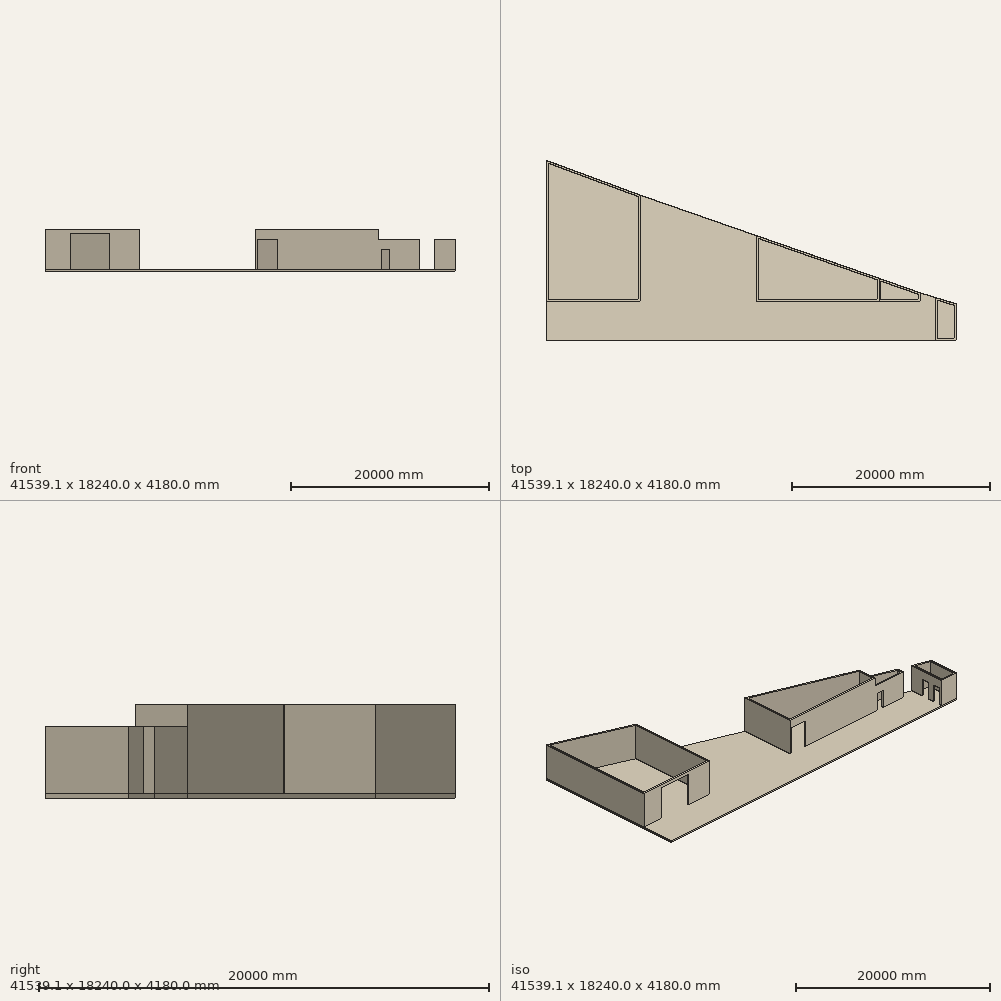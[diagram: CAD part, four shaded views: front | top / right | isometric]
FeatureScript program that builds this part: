
annotation { "Feature Type Name" : "Feature", "Feature Type Description" : "" }
export const myFeature = defineFeature(function(context is Context, id is Id, definition is map)
    precondition{}
    {
        {
            var Q0;
            Q0=qCreatedBy(makeId("Top.planeOp"),FACE);
            var sketch = newSketch(context, id + "F0", { "sketchPlane" : qUnion([Q0])});
            skLineSegment(sketch, "E0", {"start": v(-6364.4, -7586.4) * mm, "end": v(3195.6, -7586.4) * mm});
            skLineSegment(sketch, "E1", {"start": v(3195.6, -7586.4) * mm, "end": v(3195.6, 3113.6) * mm});
            skLineSegment(sketch, "E2", {"start": v(3195.6, 3113.6) * mm, "end": v(-6364.4, 6653.6) * mm});
            skLineSegment(sketch, "E3", {"start": v(-6364.4, 6653.6) * mm, "end": v(-6364.4, -7586.4) * mm});
            skLineSegment(sketch, "E4", {"start": v(14943.68, -976.4) * mm, "end": v(27323.68, -5286.4) * mm});
            skLineSegment(sketch, "E5", {"start": v(27323.68, -5286.4) * mm, "end": v(27323.68, -7586.4) * mm});
            skLineSegment(sketch, "E6", {"start": v(27323.68, -7586.4) * mm, "end": v(14943.68, -7586.4) * mm});
            skLineSegment(sketch, "E7", {"start": v(14943.68, -7586.4) * mm, "end": v(14943.68, -976.4) * mm});
            skLineSegment(sketch, "E8", {"start": v(3195.6, 3113.6) * mm, "end": v(14943.68, -976.4) * mm});
            skLineSegment(sketch, "E9", {"start": v(3195.6, -7586.4) * mm, "end": v(14943.68, -7586.4) * mm});
            skLineSegment(sketch, "E10", {"start": v(27323.68, -5286.4) * mm, "end": v(31493.68, -6756.4) * mm});
            skLineSegment(sketch, "E11", {"start": v(31493.68, -6756.4) * mm, "end": v(31493.68, -7586.4) * mm});
            skLineSegment(sketch, "E12", {"start": v(31493.68, -7586.4) * mm, "end": v(27323.68, -7586.4) * mm});
            skLineSegment(sketch, "E13", {"start": v(33024.74, -7226.4) * mm, "end": v(35174.74, -7886.4) * mm});
            skLineSegment(sketch, "E14", {"start": v(35174.74, -7886.4) * mm, "end": v(35174.74, -11586.4) * mm});
            skLineSegment(sketch, "E15", {"start": v(35174.74, -11586.4) * mm, "end": v(33024.74, -11586.4) * mm});
            skLineSegment(sketch, "E16", {"start": v(33024.74, -11586.4) * mm, "end": v(33024.74, -7226.4) * mm});
            skLineSegment(sketch, "E17", {"start": v(33024.74, -7226.4) * mm, "end": v(31493.68, -6756.4) * mm});
            skLineSegment(sketch, "E18", {"start": v(33024.74, -11586.4) * mm, "end": v(-6364.4, -11586.4) * mm});
            skLineSegment(sketch, "E19", {"start": v(-6364.4, -11586.4) * mm, "end": v(-6364.4, -7586.4) * mm});
            skSolve(sketch);
        }
        {
            var Q0;
            Q0=makeQuery(id+"F0.imprint","IMPRINT",FACE,{"disambiguationData":[TD([[makeQuery(id+"F0.imprint","IMPRINT",EDGE,{"derivedFrom":sQuery(id+"F0.wireOp",EDGE,"E0")}),1.0]])]});
            extrude(context, id + "F1", {"entities" : qUnion([Q0]), "depth" : 3980 * mm});
        }
        {
            var Q0;
            Q0=makeQuery(id+"F1.opExtrude","CAP_FACE",FACE,{"disambiguationData":[OSD([sQuery(id+"F0.wireOp",EDGE,"E0"),sQuery(id+"F0.wireOp",EDGE,"E1"),sQuery(id+"F0.wireOp",EDGE,"E2"),sQuery(id+"F0.wireOp",EDGE,"E3")])],"isStart":false});
            var sketch = newSketch(context, id + "F2", { "sketchPlane" : qUnion([Q0])});
            skLineSegment(sketch, "E20.0", {"start": v(2995.6, 2974.38) * mm, "end": v(-6164.4, 6366.26) * mm});
            skLineSegment(sketch, "E20.1", {"start": v(2995.6, -7386.4) * mm, "end": v(2995.6, 2974.38) * mm});
            skLineSegment(sketch, "E20.2", {"start": v(-6164.4, -7386.4) * mm, "end": v(2995.6, -7386.4) * mm});
            skLineSegment(sketch, "E20.3", {"start": v(-6164.4, 6366.26) * mm, "end": v(-6164.4, -7386.4) * mm});
            skSolve(sketch);
        }
        {
            var Q0;
            Q0 = qSketchRegion(id + "F2", true);
            extrude(context, id + "F3", {"entities" : qUnion([Q0]), "operationType" : NewBodyOperationType.REMOVE, "oppositeDirection" : true, "depth" : 3980 * mm});
        }
        {
            var Q0;
            Q0=makeQuery(id+"F0.imprint","IMPRINT",FACE,{"disambiguationData":[TD([[makeQuery(id+"F0.imprint","IMPRINT",EDGE,{"derivedFrom":sQuery(id+"F0.wireOp",EDGE,"E4")}),-1.0]])]});
            extrude(context, id + "F4", {"entities" : qUnion([Q0]), "depth" : 3980 * mm});
        }
        {
            var Q0;
            Q0=makeQuery(id+"F4.opExtrude","CAP_FACE",FACE,{"disambiguationData":[OSD([sQuery(id+"F0.wireOp",EDGE,"E4"),sQuery(id+"F0.wireOp",EDGE,"E5"),sQuery(id+"F0.wireOp",EDGE,"E6"),sQuery(id+"F0.wireOp",EDGE,"E7")])],"isStart":false});
            var sketch = newSketch(context, id + "F5", { "sketchPlane" : qUnion([Q0])});
            skLineSegment(sketch, "E21.0", {"start": v(15143.68, -1257.8) * mm, "end": v(15143.68, -7386.4) * mm});
            skLineSegment(sketch, "E21.1", {"start": v(27123.68, -5428.55) * mm, "end": v(15143.68, -1257.8) * mm});
            skLineSegment(sketch, "E21.2", {"start": v(27123.68, -7386.4) * mm, "end": v(27123.68, -5428.55) * mm});
            skLineSegment(sketch, "E21.3", {"start": v(15143.68, -7386.4) * mm, "end": v(27123.68, -7386.4) * mm});
            skSolve(sketch);
        }
        {
            var Q0;
            Q0=makeQuery(id+"F5.imprint","IMPRINT",FACE,{"disambiguationData":[TD([[makeQuery(id+"F5.imprint","IMPRINT",EDGE,{"derivedFrom":sQuery(id+"F5.wireOp",EDGE,"E21.0")}),1.0]])]});
            extrude(context, id + "F6", {"entities" : qUnion([Q0]), "operationType" : NewBodyOperationType.REMOVE, "oppositeDirection" : true, "depth" : 3980 * mm});
        }
        {
            var Q0;
            Q0=makeQuery(id+"F0.imprint","IMPRINT",FACE,{"disambiguationData":[TD([[makeQuery(id+"F0.imprint","IMPRINT",EDGE,{"derivedFrom":sQuery(id+"F0.wireOp",EDGE,"E5")}),1.0]])]});
            extrude(context, id + "F7", {"entities" : qUnion([Q0]), "operationType" : NewBodyOperationType.ADD, "depth" : 3000 * mm});
        }
        {
            var Q0;
            Q0=makeQuery(id+"F7.opExtrude","CAP_FACE",FACE,{"disambiguationData":[OSD([sQuery(id+"F0.wireOp",EDGE,"E5"),sQuery(id+"F0.wireOp",EDGE,"E10"),sQuery(id+"F0.wireOp",EDGE,"E11"),sQuery(id+"F0.wireOp",EDGE,"E12")])],"isStart":false});
            var sketch = newSketch(context, id + "F8", { "sketchPlane" : qUnion([Q0])});
            skLineSegment(sketch, "E22.0", {"start": v(27523.68, -7386.4) * mm, "end": v(31293.68, -7386.4) * mm});
            skLineSegment(sketch, "E22.1", {"start": v(27523.68, -5568.97) * mm, "end": v(27523.68, -7386.4) * mm});
            skLineSegment(sketch, "E22.2", {"start": v(31293.68, -6897.97) * mm, "end": v(27523.68, -5568.97) * mm});
            skLineSegment(sketch, "E22.3", {"start": v(31293.68, -7386.4) * mm, "end": v(31293.68, -6897.97) * mm});
            skSolve(sketch);
        }
        {
            var Q0;
            Q0=makeQuery(id+"F8.imprint","IMPRINT",FACE,{"disambiguationData":[TD([[makeQuery(id+"F8.imprint","IMPRINT",EDGE,{"derivedFrom":sQuery(id+"F8.wireOp",EDGE,"E22.0")}),1.0]])]});
            extrude(context, id + "F9", {"entities" : qUnion([Q0]), "operationType" : NewBodyOperationType.REMOVE, "oppositeDirection" : true, "depth" : 3000 * mm});
        }
        {
            var Q0;
            Q0=makeQuery(id+"F1.opExtrude","SWEPT_FACE",FACE,{"disambiguationData":[OSD([sQuery(id+"F0.wireOp",EDGE,"E0")])]});
            var sketch = newSketch(context, id + "F10", { "sketchPlane" : qUnion([Q0])});
            skLineSegment(sketch, "E23.bottom", {"start": v(-3864.4, 0) * mm, "end": v(135.6, 0) * mm});
            skLineSegment(sketch, "E23.top", {"start": v(-3864.4, 3600) * mm, "end": v(135.6, 3600) * mm});
            skLineSegment(sketch, "E23.left", {"start": v(-3864.4, 0) * mm, "end": v(-3864.4, 3600) * mm});
            skLineSegment(sketch, "E23.right", {"start": v(135.6, 0) * mm, "end": v(135.6, 3600) * mm});
            skSolve(sketch);
        }
        {
            var Q0;
            Q0=makeQuery(id+"F10.imprint","IMPRINT",FACE,{"disambiguationData":[TD([[makeQuery(id+"F10.imprint","IMPRINT",EDGE,{"derivedFrom":sQuery(id+"F10.wireOp",EDGE,"E23.bottom")}),1.0]])]});
            extrude(context, id + "F11", {"entities" : qUnion([Q0]), "operationType" : NewBodyOperationType.REMOVE, "endBound" : BoundingType.UP_TO_NEXT, "oppositeDirection" : true, "depth" : 25 * mm});
        }
        {
            var Q0;
            Q0=makeQuery(id+"F7.boolean.opBoolean","MERGE",FACE,{"derivedFrom":[makeQuery(id+"F4.opExtrude","SWEPT_FACE",FACE,{"disambiguationData":[OSD([sQuery(id+"F0.wireOp",EDGE,"E6")])]}),makeQuery(id+"F7.opExtrude","SWEPT_FACE",FACE,{"disambiguationData":[OSD([sQuery(id+"F0.wireOp",EDGE,"E12")])]})]});
            var sketch = newSketch(context, id + "F12", { "sketchPlane" : qUnion([Q0])});
            skLineSegment(sketch, "E24.bottom", {"start": v(15143.68, 0) * mm, "end": v(17143.68, 0) * mm});
            skLineSegment(sketch, "E24.top", {"start": v(15143.68, 3000) * mm, "end": v(17143.68, 3000) * mm});
            skLineSegment(sketch, "E24.left", {"start": v(15143.68, 0) * mm, "end": v(15143.68, 3000) * mm});
            skLineSegment(sketch, "E24.right", {"start": v(17143.68, 0) * mm, "end": v(17143.68, 3000) * mm});
            skLineSegment(sketch, "E25.bottom", {"start": v(27693.68, 0) * mm, "end": v(28493.68, 0) * mm});
            skLineSegment(sketch, "E25.top", {"start": v(27693.68, 2000) * mm, "end": v(28493.68, 2000) * mm});
            skLineSegment(sketch, "E25.left", {"start": v(27693.68, 0) * mm, "end": v(27693.68, 2000) * mm});
            skLineSegment(sketch, "E25.right", {"start": v(28493.68, 0) * mm, "end": v(28493.68, 2000) * mm});
            skSolve(sketch);
        }
        {
            var Q0;
            Q0=makeQuery(id+"F12.imprint","IMPRINT",FACE,{"disambiguationData":[TD([[makeQuery(id+"F12.imprint","IMPRINT",EDGE,{"derivedFrom":sQuery(id+"F12.wireOp",EDGE,"E24.bottom")}),-1.0]])]});
            extrude(context, id + "F13", {"entities" : qUnion([Q0]), "operationType" : NewBodyOperationType.REMOVE, "endBound" : BoundingType.UP_TO_NEXT, "oppositeDirection" : true, "depth" : 25 * mm});
        }
        {
            var Q0;
            Q0=makeQuery(id+"F12.imprint","IMPRINT",FACE,{"disambiguationData":[TD([[makeQuery(id+"F12.imprint","IMPRINT",EDGE,{"derivedFrom":sQuery(id+"F12.wireOp",EDGE,"E25.bottom")}),-1.0]])]});
            extrude(context, id + "F14", {"entities" : qUnion([Q0]), "operationType" : NewBodyOperationType.REMOVE, "endBound" : BoundingType.UP_TO_NEXT, "oppositeDirection" : true, "depth" : 25 * mm});
        }
        {
            var Q0;
            Q0=makeQuery(id+"F0.imprint","IMPRINT",FACE,{"disambiguationData":[TD([[makeQuery(id+"F0.imprint","IMPRINT",EDGE,{"derivedFrom":sQuery(id+"F0.wireOp",EDGE,"E13")}),-1.0]])]});
            extrude(context, id + "F15", {"entities" : qUnion([Q0]), "depth" : 3000 * mm});
        }
        {
            var Q0;
            Q0=makeQuery(id+"F15.opExtrude","CAP_FACE",FACE,{"disambiguationData":[OSD([sQuery(id+"F0.wireOp",EDGE,"E13"),sQuery(id+"F0.wireOp",EDGE,"E14"),sQuery(id+"F0.wireOp",EDGE,"E15"),sQuery(id+"F0.wireOp",EDGE,"E16")])],"isStart":false});
            var sketch = newSketch(context, id + "F16", { "sketchPlane" : qUnion([Q0])});
            skLineSegment(sketch, "E26.0", {"start": v(33224.74, -7497.01) * mm, "end": v(33224.74, -11386.4) * mm});
            skLineSegment(sketch, "E26.1", {"start": v(34974.74, -8034.22) * mm, "end": v(33224.74, -7497.01) * mm});
            skLineSegment(sketch, "E26.2", {"start": v(34974.74, -11386.4) * mm, "end": v(34974.74, -8034.22) * mm});
            skLineSegment(sketch, "E26.3", {"start": v(33224.74, -11386.4) * mm, "end": v(34974.74, -11386.4) * mm});
            skSolve(sketch);
        }
        {
            var Q0;
            Q0 = qSketchRegion(id + "F16", true);
            extrude(context, id + "F17", {"entities" : qUnion([Q0]), "operationType" : NewBodyOperationType.REMOVE, "oppositeDirection" : true, "depth" : 3000 * mm});
        }
        {
            var Q0;
            Q0=makeQuery(id+"F15.opExtrude","SWEPT_FACE",FACE,{"disambiguationData":[OSD([sQuery(id+"F0.wireOp",EDGE,"E16")])]});
            var sketch = newSketch(context, id + "F18", { "sketchPlane" : qUnion([Q0])});
            skLineSegment(sketch, "E27.bottom", {"start": v(11186.4, 0) * mm, "end": v(10386.4, 0) * mm});
            skLineSegment(sketch, "E27.top", {"start": v(11186.4, 2000) * mm, "end": v(10386.4, 2000) * mm});
            skLineSegment(sketch, "E27.left", {"start": v(11186.4, 0) * mm, "end": v(11186.4, 2000) * mm});
            skLineSegment(sketch, "E27.right", {"start": v(10386.4, 0) * mm, "end": v(10386.4, 2000) * mm});
            skLineSegment(sketch, "E28.bottom", {"start": v(9586.4, 0) * mm, "end": v(8786.4, 0) * mm});
            skLineSegment(sketch, "E28.top", {"start": v(9586.4, 2000) * mm, "end": v(8786.4, 2000) * mm});
            skLineSegment(sketch, "E28.left", {"start": v(9586.4, 0) * mm, "end": v(9586.4, 2000) * mm});
            skLineSegment(sketch, "E28.right", {"start": v(8786.4, 0) * mm, "end": v(8786.4, 2000) * mm});
            skSolve(sketch);
        }
        {
            var Q0;
            Q0=makeQuery(id+"F18.imprint","IMPRINT",FACE,{"disambiguationData":[TD([[makeQuery(id+"F18.imprint","IMPRINT",EDGE,{"derivedFrom":sQuery(id+"F18.wireOp",EDGE,"E28.bottom")}),-1.0]])]});
            var Q1;
            Q1=makeQuery(id+"F18.imprint","IMPRINT",FACE,{"disambiguationData":[TD([[makeQuery(id+"F18.imprint","IMPRINT",EDGE,{"derivedFrom":sQuery(id+"F18.wireOp",EDGE,"E27.bottom")}),-1.0]])]});
            extrude(context, id + "F19", {"entities" : qUnion([Q0, Q1]), "operationType" : NewBodyOperationType.REMOVE, "endBound" : BoundingType.UP_TO_NEXT, "oppositeDirection" : true, "depth" : 25 * mm});
        }
        {
            var Q0;
            Q0=makeQuery(id+"F0.imprint","IMPRINT",FACE,{"disambiguationData":[TD([[makeQuery(id+"F0.imprint","IMPRINT",EDGE,{"derivedFrom":sQuery(id+"F0.wireOp",EDGE,"E0")}),-1.0]])]});
            var Q1;
            Q1=makeQuery(id+"F0.imprint","IMPRINT",FACE,{"disambiguationData":[TD([[makeQuery(id+"F0.imprint","IMPRINT",EDGE,{"derivedFrom":sQuery(id+"F0.wireOp",EDGE,"E13")}),-1.0]])]});
            var Q2;
            Q2=makeQuery(id+"F0.imprint","IMPRINT",FACE,{"disambiguationData":[TD([[makeQuery(id+"F0.imprint","IMPRINT",EDGE,{"derivedFrom":sQuery(id+"F0.wireOp",EDGE,"E5")}),1.0]])]});
            var Q3;
            Q3=makeQuery(id+"F0.imprint","IMPRINT",FACE,{"disambiguationData":[TD([[makeQuery(id+"F0.imprint","IMPRINT",EDGE,{"derivedFrom":sQuery(id+"F0.wireOp",EDGE,"E4")}),-1.0]])]});
            var Q4;
            Q4=makeQuery(id+"F0.imprint","IMPRINT",FACE,{"disambiguationData":[TD([[makeQuery(id+"F0.imprint","IMPRINT",EDGE,{"derivedFrom":sQuery(id+"F0.wireOp",EDGE,"E1")}),-1.0]])]});
            var Q5;
            Q5=makeQuery(id+"F0.imprint","IMPRINT",FACE,{"disambiguationData":[TD([[makeQuery(id+"F0.imprint","IMPRINT",EDGE,{"derivedFrom":sQuery(id+"F0.wireOp",EDGE,"E0")}),1.0]])]});
            extrude(context, id + "F20", {"entities" : qUnion([Q0, Q1, Q2, Q3, Q4, Q5]), "oppositeDirection" : true, "depth" : 200 * mm});
        }
    });
